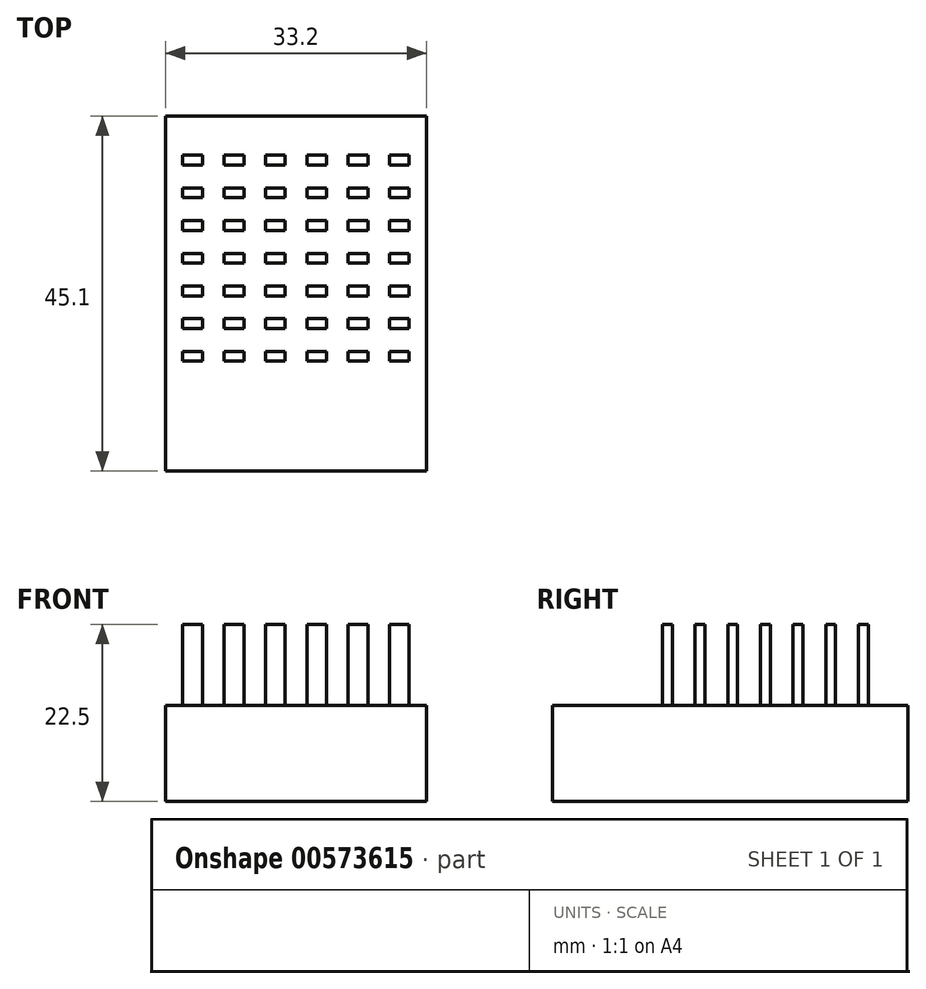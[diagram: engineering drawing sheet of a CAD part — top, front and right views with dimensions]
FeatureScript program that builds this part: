
annotation { "Feature Type Name" : "Feature", "Feature Type Description" : "" }
export const myFeature = defineFeature(function(context is Context, id is Id, definition is map)
    precondition{}
    {
        {
            var Q0;
            Q0=qCreatedBy(makeId("Top.planeOp"),FACE);
            var sketch = newSketch(context, id + "F0", { "sketchPlane" : qUnion([Q0])});
            skLineSegment(sketch, "E0.bottom", {"start": v(16.6, -22.55) * mm, "end": v(-16.6, -22.55) * mm});
            skLineSegment(sketch, "E0.top", {"start": v(16.6, 22.55) * mm, "end": v(-16.6, 22.55) * mm});
            skLineSegment(sketch, "E0.left", {"start": v(16.6, -22.55) * mm, "end": v(16.6, 22.55) * mm});
            skLineSegment(sketch, "E0.right", {"start": v(-16.6, -22.55) * mm, "end": v(-16.6, 22.55) * mm});
            skPoint(sketch, "E0.middle", {"position": v(0, 0) * mm});
            skSolve(sketch);
        }
        {
            var Q0;
            Q0 = qSketchRegion(id + "F0", true);
            extrude(context, id + "F1", {"entities" : qUnion([Q0]), "depth" : 12.2 * mm, "offsetDistance" : 25 * mm});
        }
        {
            var Q0;
            Q0=makeQuery(id+"F1.opExtrude","CAP_FACE",FACE,{"disambiguationData":[OSD([sQuery(id+"F0.wireOp",EDGE,"E0.bottom"),sQuery(id+"F0.wireOp",EDGE,"E0.top"),sQuery(id+"F0.wireOp",EDGE,"E0.left"),sQuery(id+"F0.wireOp",EDGE,"E0.right")])],"isStart":false});
            var sketch = newSketch(context, id + "F2", { "sketchPlane" : qUnion([Q0])});
            skLineSegment(sketch, "E1.bottom", {"start": v(-11.88, 16.3) * mm, "end": v(-14.38, 16.3) * mm});
            skLineSegment(sketch, "E1.top", {"start": v(-11.88, 17.55) * mm, "end": v(-14.38, 17.55) * mm});
            skLineSegment(sketch, "E1.left", {"start": v(-11.88, 16.3) * mm, "end": v(-11.88, 17.55) * mm});
            skLineSegment(sketch, "E1.right", {"start": v(-14.38, 16.3) * mm, "end": v(-14.38, 17.55) * mm});
            skPoint(sketch, "E1.middle", {"position": v(-13.13, 16.93) * mm});
            skPoint(sketch, "E2.0.1.0", {"position": v(-13.13, 12.78) * mm});
            skLineSegment(sketch, "E2.0.1.1", {"start": v(-11.88, 13.4) * mm, "end": v(-14.38, 13.4) * mm});
            skLineSegment(sketch, "E2.0.1.2", {"start": v(-11.88, 12.15) * mm, "end": v(-14.38, 12.15) * mm});
            skLineSegment(sketch, "E2.0.1.3", {"start": v(-14.38, 12.15) * mm, "end": v(-14.38, 13.4) * mm});
            skLineSegment(sketch, "E2.0.1.4", {"start": v(-11.88, 12.15) * mm, "end": v(-11.88, 13.4) * mm});
            skPoint(sketch, "E2.0.2.0", {"position": v(-13.13, 8.62) * mm});
            skLineSegment(sketch, "E2.0.2.1", {"start": v(-11.88, 9.25) * mm, "end": v(-14.38, 9.25) * mm});
            skLineSegment(sketch, "E2.0.2.2", {"start": v(-11.88, 8) * mm, "end": v(-14.38, 8) * mm});
            skLineSegment(sketch, "E2.0.2.3", {"start": v(-14.38, 8) * mm, "end": v(-14.38, 9.25) * mm});
            skLineSegment(sketch, "E2.0.2.4", {"start": v(-11.88, 8) * mm, "end": v(-11.88, 9.25) * mm});
            skPoint(sketch, "E2.0.3.0", {"position": v(-13.13, 4.47) * mm});
            skLineSegment(sketch, "E2.0.3.1", {"start": v(-11.88, 5.1) * mm, "end": v(-14.38, 5.1) * mm});
            skLineSegment(sketch, "E2.0.3.2", {"start": v(-11.88, 3.85) * mm, "end": v(-14.38, 3.85) * mm});
            skLineSegment(sketch, "E2.0.3.3", {"start": v(-14.38, 3.85) * mm, "end": v(-14.38, 5.1) * mm});
            skLineSegment(sketch, "E2.0.3.4", {"start": v(-11.88, 3.85) * mm, "end": v(-11.88, 5.1) * mm});
            skPoint(sketch, "E2.0.4.0", {"position": v(-13.13, 0.32) * mm});
            skLineSegment(sketch, "E2.0.4.1", {"start": v(-11.88, 0.95) * mm, "end": v(-14.38, 0.95) * mm});
            skLineSegment(sketch, "E2.0.4.2", {"start": v(-11.88, -0.3) * mm, "end": v(-14.38, -0.3) * mm});
            skLineSegment(sketch, "E2.0.4.3", {"start": v(-14.38, -0.3) * mm, "end": v(-14.38, 0.95) * mm});
            skLineSegment(sketch, "E2.0.4.4", {"start": v(-11.88, -0.3) * mm, "end": v(-11.88, 0.95) * mm});
            skPoint(sketch, "E2.0.5.0", {"position": v(-13.13, -3.83) * mm});
            skLineSegment(sketch, "E2.0.5.1", {"start": v(-11.88, -3.2) * mm, "end": v(-14.38, -3.2) * mm});
            skLineSegment(sketch, "E2.0.5.2", {"start": v(-11.88, -4.45) * mm, "end": v(-14.38, -4.45) * mm});
            skLineSegment(sketch, "E2.0.5.3", {"start": v(-14.38, -4.45) * mm, "end": v(-14.38, -3.2) * mm});
            skLineSegment(sketch, "E2.0.5.4", {"start": v(-11.88, -4.45) * mm, "end": v(-11.88, -3.2) * mm});
            skPoint(sketch, "E2.0.6.0", {"position": v(-13.13, -7.98) * mm});
            skLineSegment(sketch, "E2.0.6.1", {"start": v(-11.88, -7.35) * mm, "end": v(-14.38, -7.35) * mm});
            skLineSegment(sketch, "E2.0.6.2", {"start": v(-11.88, -8.6) * mm, "end": v(-14.38, -8.6) * mm});
            skLineSegment(sketch, "E2.0.6.3", {"start": v(-14.38, -8.6) * mm, "end": v(-14.38, -7.35) * mm});
            skLineSegment(sketch, "E2.0.6.4", {"start": v(-11.88, -8.6) * mm, "end": v(-11.88, -7.35) * mm});
            skPoint(sketch, "E2.1.0.0", {"position": v(-7.88, 16.93) * mm});
            skLineSegment(sketch, "E2.1.0.1", {"start": v(-6.63, 17.55) * mm, "end": v(-9.13, 17.55) * mm});
            skLineSegment(sketch, "E2.1.0.2", {"start": v(-6.63, 16.3) * mm, "end": v(-9.13, 16.3) * mm});
            skLineSegment(sketch, "E2.1.0.3", {"start": v(-9.13, 16.3) * mm, "end": v(-9.13, 17.55) * mm});
            skLineSegment(sketch, "E2.1.0.4", {"start": v(-6.63, 16.3) * mm, "end": v(-6.63, 17.55) * mm});
            skPoint(sketch, "E2.1.1.0", {"position": v(-7.88, 12.78) * mm});
            skLineSegment(sketch, "E2.1.1.1", {"start": v(-6.63, 13.4) * mm, "end": v(-9.13, 13.4) * mm});
            skLineSegment(sketch, "E2.1.1.2", {"start": v(-6.63, 12.15) * mm, "end": v(-9.13, 12.15) * mm});
            skLineSegment(sketch, "E2.1.1.3", {"start": v(-9.13, 12.15) * mm, "end": v(-9.13, 13.4) * mm});
            skLineSegment(sketch, "E2.1.1.4", {"start": v(-6.63, 12.15) * mm, "end": v(-6.63, 13.4) * mm});
            skPoint(sketch, "E2.1.2.0", {"position": v(-7.88, 8.62) * mm});
            skLineSegment(sketch, "E2.1.2.1", {"start": v(-6.63, 9.25) * mm, "end": v(-9.13, 9.25) * mm});
            skLineSegment(sketch, "E2.1.2.2", {"start": v(-6.63, 8) * mm, "end": v(-9.13, 8) * mm});
            skLineSegment(sketch, "E2.1.2.3", {"start": v(-9.13, 8) * mm, "end": v(-9.13, 9.25) * mm});
            skLineSegment(sketch, "E2.1.2.4", {"start": v(-6.63, 8) * mm, "end": v(-6.63, 9.25) * mm});
            skPoint(sketch, "E2.1.3.0", {"position": v(-7.88, 4.47) * mm});
            skLineSegment(sketch, "E2.1.3.1", {"start": v(-6.63, 5.1) * mm, "end": v(-9.13, 5.1) * mm});
            skLineSegment(sketch, "E2.1.3.2", {"start": v(-6.63, 3.85) * mm, "end": v(-9.13, 3.85) * mm});
            skLineSegment(sketch, "E2.1.3.3", {"start": v(-9.13, 3.85) * mm, "end": v(-9.13, 5.1) * mm});
            skLineSegment(sketch, "E2.1.3.4", {"start": v(-6.63, 3.85) * mm, "end": v(-6.63, 5.1) * mm});
            skPoint(sketch, "E2.1.4.0", {"position": v(-7.88, 0.32) * mm});
            skLineSegment(sketch, "E2.1.4.1", {"start": v(-6.63, 0.95) * mm, "end": v(-9.13, 0.95) * mm});
            skLineSegment(sketch, "E2.1.4.2", {"start": v(-6.63, -0.3) * mm, "end": v(-9.13, -0.3) * mm});
            skLineSegment(sketch, "E2.1.4.3", {"start": v(-9.13, -0.3) * mm, "end": v(-9.13, 0.95) * mm});
            skLineSegment(sketch, "E2.1.4.4", {"start": v(-6.63, -0.3) * mm, "end": v(-6.63, 0.95) * mm});
            skPoint(sketch, "E2.1.5.0", {"position": v(-7.88, -3.83) * mm});
            skLineSegment(sketch, "E2.1.5.1", {"start": v(-6.63, -3.2) * mm, "end": v(-9.13, -3.2) * mm});
            skLineSegment(sketch, "E2.1.5.2", {"start": v(-6.63, -4.45) * mm, "end": v(-9.13, -4.45) * mm});
            skLineSegment(sketch, "E2.1.5.3", {"start": v(-9.13, -4.45) * mm, "end": v(-9.13, -3.2) * mm});
            skLineSegment(sketch, "E2.1.5.4", {"start": v(-6.63, -4.45) * mm, "end": v(-6.63, -3.2) * mm});
            skPoint(sketch, "E2.1.6.0", {"position": v(-7.88, -7.98) * mm});
            skLineSegment(sketch, "E2.1.6.1", {"start": v(-6.63, -7.35) * mm, "end": v(-9.13, -7.35) * mm});
            skLineSegment(sketch, "E2.1.6.2", {"start": v(-6.63, -8.6) * mm, "end": v(-9.13, -8.6) * mm});
            skLineSegment(sketch, "E2.1.6.3", {"start": v(-9.13, -8.6) * mm, "end": v(-9.13, -7.35) * mm});
            skLineSegment(sketch, "E2.1.6.4", {"start": v(-6.63, -8.6) * mm, "end": v(-6.63, -7.35) * mm});
            skPoint(sketch, "E2.2.0.0", {"position": v(-2.62, 16.93) * mm});
            skLineSegment(sketch, "E2.2.0.1", {"start": v(-1.37, 17.55) * mm, "end": v(-3.88, 17.55) * mm});
            skLineSegment(sketch, "E2.2.0.2", {"start": v(-1.37, 16.3) * mm, "end": v(-3.88, 16.3) * mm});
            skLineSegment(sketch, "E2.2.0.3", {"start": v(-3.88, 16.3) * mm, "end": v(-3.88, 17.55) * mm});
            skLineSegment(sketch, "E2.2.0.4", {"start": v(-1.38, 16.3) * mm, "end": v(-1.38, 17.55) * mm});
            skPoint(sketch, "E2.2.1.0", {"position": v(-2.62, 12.78) * mm});
            skLineSegment(sketch, "E2.2.1.1", {"start": v(-1.37, 13.4) * mm, "end": v(-3.88, 13.4) * mm});
            skLineSegment(sketch, "E2.2.1.2", {"start": v(-1.37, 12.15) * mm, "end": v(-3.88, 12.15) * mm});
            skLineSegment(sketch, "E2.2.1.3", {"start": v(-3.88, 12.15) * mm, "end": v(-3.88, 13.4) * mm});
            skLineSegment(sketch, "E2.2.1.4", {"start": v(-1.38, 12.15) * mm, "end": v(-1.38, 13.4) * mm});
            skPoint(sketch, "E2.2.2.0", {"position": v(-2.62, 8.62) * mm});
            skLineSegment(sketch, "E2.2.2.1", {"start": v(-1.37, 9.25) * mm, "end": v(-3.88, 9.25) * mm});
            skLineSegment(sketch, "E2.2.2.2", {"start": v(-1.37, 8) * mm, "end": v(-3.88, 8) * mm});
            skLineSegment(sketch, "E2.2.2.3", {"start": v(-3.88, 8) * mm, "end": v(-3.88, 9.25) * mm});
            skLineSegment(sketch, "E2.2.2.4", {"start": v(-1.38, 8) * mm, "end": v(-1.38, 9.25) * mm});
            skPoint(sketch, "E2.2.3.0", {"position": v(-2.62, 4.47) * mm});
            skLineSegment(sketch, "E2.2.3.1", {"start": v(-1.37, 5.1) * mm, "end": v(-3.88, 5.1) * mm});
            skLineSegment(sketch, "E2.2.3.2", {"start": v(-1.37, 3.85) * mm, "end": v(-3.88, 3.85) * mm});
            skLineSegment(sketch, "E2.2.3.3", {"start": v(-3.88, 3.85) * mm, "end": v(-3.88, 5.1) * mm});
            skLineSegment(sketch, "E2.2.3.4", {"start": v(-1.38, 3.85) * mm, "end": v(-1.38, 5.1) * mm});
            skPoint(sketch, "E2.2.4.0", {"position": v(-2.62, 0.32) * mm});
            skLineSegment(sketch, "E2.2.4.1", {"start": v(-1.37, 0.95) * mm, "end": v(-3.88, 0.95) * mm});
            skLineSegment(sketch, "E2.2.4.2", {"start": v(-1.37, -0.3) * mm, "end": v(-3.88, -0.3) * mm});
            skLineSegment(sketch, "E2.2.4.3", {"start": v(-3.88, -0.3) * mm, "end": v(-3.88, 0.95) * mm});
            skLineSegment(sketch, "E2.2.4.4", {"start": v(-1.38, -0.3) * mm, "end": v(-1.38, 0.95) * mm});
            skPoint(sketch, "E2.2.5.0", {"position": v(-2.62, -3.83) * mm});
            skLineSegment(sketch, "E2.2.5.1", {"start": v(-1.37, -3.2) * mm, "end": v(-3.88, -3.2) * mm});
            skLineSegment(sketch, "E2.2.5.2", {"start": v(-1.37, -4.45) * mm, "end": v(-3.88, -4.45) * mm});
            skLineSegment(sketch, "E2.2.5.3", {"start": v(-3.88, -4.45) * mm, "end": v(-3.88, -3.2) * mm});
            skLineSegment(sketch, "E2.2.5.4", {"start": v(-1.38, -4.45) * mm, "end": v(-1.38, -3.2) * mm});
            skPoint(sketch, "E2.2.6.0", {"position": v(-2.62, -7.98) * mm});
            skLineSegment(sketch, "E2.2.6.1", {"start": v(-1.37, -7.35) * mm, "end": v(-3.88, -7.35) * mm});
            skLineSegment(sketch, "E2.2.6.2", {"start": v(-1.37, -8.6) * mm, "end": v(-3.88, -8.6) * mm});
            skLineSegment(sketch, "E2.2.6.3", {"start": v(-3.88, -8.6) * mm, "end": v(-3.88, -7.35) * mm});
            skLineSegment(sketch, "E2.2.6.4", {"start": v(-1.38, -8.6) * mm, "end": v(-1.38, -7.35) * mm});
            skPoint(sketch, "E2.3.0.0", {"position": v(2.63, 16.93) * mm});
            skLineSegment(sketch, "E2.3.0.1", {"start": v(3.88, 17.55) * mm, "end": v(1.38, 17.55) * mm});
            skLineSegment(sketch, "E2.3.0.2", {"start": v(3.88, 16.3) * mm, "end": v(1.38, 16.3) * mm});
            skLineSegment(sketch, "E2.3.0.3", {"start": v(1.37, 16.3) * mm, "end": v(1.37, 17.55) * mm});
            skLineSegment(sketch, "E2.3.0.4", {"start": v(3.87, 16.3) * mm, "end": v(3.87, 17.55) * mm});
            skPoint(sketch, "E2.3.1.0", {"position": v(2.63, 12.78) * mm});
            skLineSegment(sketch, "E2.3.1.1", {"start": v(3.88, 13.4) * mm, "end": v(1.38, 13.4) * mm});
            skLineSegment(sketch, "E2.3.1.2", {"start": v(3.88, 12.15) * mm, "end": v(1.38, 12.15) * mm});
            skLineSegment(sketch, "E2.3.1.3", {"start": v(1.37, 12.15) * mm, "end": v(1.37, 13.4) * mm});
            skLineSegment(sketch, "E2.3.1.4", {"start": v(3.87, 12.15) * mm, "end": v(3.87, 13.4) * mm});
            skPoint(sketch, "E2.3.2.0", {"position": v(2.63, 8.62) * mm});
            skLineSegment(sketch, "E2.3.2.1", {"start": v(3.88, 9.25) * mm, "end": v(1.38, 9.25) * mm});
            skLineSegment(sketch, "E2.3.2.2", {"start": v(3.88, 8) * mm, "end": v(1.38, 8) * mm});
            skLineSegment(sketch, "E2.3.2.3", {"start": v(1.37, 8) * mm, "end": v(1.37, 9.25) * mm});
            skLineSegment(sketch, "E2.3.2.4", {"start": v(3.87, 8) * mm, "end": v(3.87, 9.25) * mm});
            skPoint(sketch, "E2.3.3.0", {"position": v(2.63, 4.47) * mm});
            skLineSegment(sketch, "E2.3.3.1", {"start": v(3.88, 5.1) * mm, "end": v(1.38, 5.1) * mm});
            skLineSegment(sketch, "E2.3.3.2", {"start": v(3.88, 3.85) * mm, "end": v(1.38, 3.85) * mm});
            skLineSegment(sketch, "E2.3.3.3", {"start": v(1.37, 3.85) * mm, "end": v(1.37, 5.1) * mm});
            skLineSegment(sketch, "E2.3.3.4", {"start": v(3.87, 3.85) * mm, "end": v(3.87, 5.1) * mm});
            skPoint(sketch, "E2.3.4.0", {"position": v(2.63, 0.32) * mm});
            skLineSegment(sketch, "E2.3.4.1", {"start": v(3.88, 0.95) * mm, "end": v(1.38, 0.95) * mm});
            skLineSegment(sketch, "E2.3.4.2", {"start": v(3.88, -0.3) * mm, "end": v(1.38, -0.3) * mm});
            skLineSegment(sketch, "E2.3.4.3", {"start": v(1.37, -0.3) * mm, "end": v(1.37, 0.95) * mm});
            skLineSegment(sketch, "E2.3.4.4", {"start": v(3.87, -0.3) * mm, "end": v(3.87, 0.95) * mm});
            skPoint(sketch, "E2.3.5.0", {"position": v(2.63, -3.83) * mm});
            skLineSegment(sketch, "E2.3.5.1", {"start": v(3.88, -3.2) * mm, "end": v(1.38, -3.2) * mm});
            skLineSegment(sketch, "E2.3.5.2", {"start": v(3.88, -4.45) * mm, "end": v(1.38, -4.45) * mm});
            skLineSegment(sketch, "E2.3.5.3", {"start": v(1.37, -4.45) * mm, "end": v(1.37, -3.2) * mm});
            skLineSegment(sketch, "E2.3.5.4", {"start": v(3.87, -4.45) * mm, "end": v(3.87, -3.2) * mm});
            skPoint(sketch, "E2.3.6.0", {"position": v(2.63, -7.98) * mm});
            skLineSegment(sketch, "E2.3.6.1", {"start": v(3.88, -7.35) * mm, "end": v(1.38, -7.35) * mm});
            skLineSegment(sketch, "E2.3.6.2", {"start": v(3.88, -8.6) * mm, "end": v(1.38, -8.6) * mm});
            skLineSegment(sketch, "E2.3.6.3", {"start": v(1.37, -8.6) * mm, "end": v(1.37, -7.35) * mm});
            skLineSegment(sketch, "E2.3.6.4", {"start": v(3.87, -8.6) * mm, "end": v(3.87, -7.35) * mm});
            skPoint(sketch, "E2.4.0.0", {"position": v(7.88, 16.93) * mm});
            skLineSegment(sketch, "E2.4.0.1", {"start": v(9.13, 17.55) * mm, "end": v(6.63, 17.55) * mm});
            skLineSegment(sketch, "E2.4.0.2", {"start": v(9.13, 16.3) * mm, "end": v(6.63, 16.3) * mm});
            skLineSegment(sketch, "E2.4.0.3", {"start": v(6.62, 16.3) * mm, "end": v(6.62, 17.55) * mm});
            skLineSegment(sketch, "E2.4.0.4", {"start": v(9.12, 16.3) * mm, "end": v(9.12, 17.55) * mm});
            skPoint(sketch, "E2.4.1.0", {"position": v(7.88, 12.78) * mm});
            skLineSegment(sketch, "E2.4.1.1", {"start": v(9.13, 13.4) * mm, "end": v(6.63, 13.4) * mm});
            skLineSegment(sketch, "E2.4.1.2", {"start": v(9.13, 12.15) * mm, "end": v(6.63, 12.15) * mm});
            skLineSegment(sketch, "E2.4.1.3", {"start": v(6.62, 12.15) * mm, "end": v(6.62, 13.4) * mm});
            skLineSegment(sketch, "E2.4.1.4", {"start": v(9.12, 12.15) * mm, "end": v(9.12, 13.4) * mm});
            skPoint(sketch, "E2.4.2.0", {"position": v(7.88, 8.62) * mm});
            skLineSegment(sketch, "E2.4.2.1", {"start": v(9.13, 9.25) * mm, "end": v(6.63, 9.25) * mm});
            skLineSegment(sketch, "E2.4.2.2", {"start": v(9.13, 8) * mm, "end": v(6.63, 8) * mm});
            skLineSegment(sketch, "E2.4.2.3", {"start": v(6.62, 8) * mm, "end": v(6.62, 9.25) * mm});
            skLineSegment(sketch, "E2.4.2.4", {"start": v(9.12, 8) * mm, "end": v(9.12, 9.25) * mm});
            skPoint(sketch, "E2.4.3.0", {"position": v(7.88, 4.47) * mm});
            skLineSegment(sketch, "E2.4.3.1", {"start": v(9.13, 5.1) * mm, "end": v(6.63, 5.1) * mm});
            skLineSegment(sketch, "E2.4.3.2", {"start": v(9.13, 3.85) * mm, "end": v(6.63, 3.85) * mm});
            skLineSegment(sketch, "E2.4.3.3", {"start": v(6.62, 3.85) * mm, "end": v(6.62, 5.1) * mm});
            skLineSegment(sketch, "E2.4.3.4", {"start": v(9.12, 3.85) * mm, "end": v(9.12, 5.1) * mm});
            skPoint(sketch, "E2.4.4.0", {"position": v(7.88, 0.32) * mm});
            skLineSegment(sketch, "E2.4.4.1", {"start": v(9.13, 0.95) * mm, "end": v(6.63, 0.95) * mm});
            skLineSegment(sketch, "E2.4.4.2", {"start": v(9.13, -0.3) * mm, "end": v(6.63, -0.3) * mm});
            skLineSegment(sketch, "E2.4.4.3", {"start": v(6.62, -0.3) * mm, "end": v(6.62, 0.95) * mm});
            skLineSegment(sketch, "E2.4.4.4", {"start": v(9.12, -0.3) * mm, "end": v(9.12, 0.95) * mm});
            skPoint(sketch, "E2.4.5.0", {"position": v(7.88, -3.83) * mm});
            skLineSegment(sketch, "E2.4.5.1", {"start": v(9.13, -3.2) * mm, "end": v(6.63, -3.2) * mm});
            skLineSegment(sketch, "E2.4.5.2", {"start": v(9.13, -4.45) * mm, "end": v(6.63, -4.45) * mm});
            skLineSegment(sketch, "E2.4.5.3", {"start": v(6.62, -4.45) * mm, "end": v(6.62, -3.2) * mm});
            skLineSegment(sketch, "E2.4.5.4", {"start": v(9.12, -4.45) * mm, "end": v(9.12, -3.2) * mm});
            skPoint(sketch, "E2.4.6.0", {"position": v(7.88, -7.98) * mm});
            skLineSegment(sketch, "E2.4.6.1", {"start": v(9.13, -7.35) * mm, "end": v(6.63, -7.35) * mm});
            skLineSegment(sketch, "E2.4.6.2", {"start": v(9.13, -8.6) * mm, "end": v(6.63, -8.6) * mm});
            skLineSegment(sketch, "E2.4.6.3", {"start": v(6.62, -8.6) * mm, "end": v(6.62, -7.35) * mm});
            skLineSegment(sketch, "E2.4.6.4", {"start": v(9.12, -8.6) * mm, "end": v(9.12, -7.35) * mm});
            skPoint(sketch, "E2.5.0.0", {"position": v(13.13, 16.93) * mm});
            skLineSegment(sketch, "E2.5.0.1", {"start": v(14.38, 17.55) * mm, "end": v(11.88, 17.55) * mm});
            skLineSegment(sketch, "E2.5.0.2", {"start": v(14.38, 16.3) * mm, "end": v(11.88, 16.3) * mm});
            skLineSegment(sketch, "E2.5.0.3", {"start": v(11.87, 16.3) * mm, "end": v(11.87, 17.55) * mm});
            skLineSegment(sketch, "E2.5.0.4", {"start": v(14.37, 16.3) * mm, "end": v(14.37, 17.55) * mm});
            skPoint(sketch, "E2.5.1.0", {"position": v(13.13, 12.78) * mm});
            skLineSegment(sketch, "E2.5.1.1", {"start": v(14.38, 13.4) * mm, "end": v(11.88, 13.4) * mm});
            skLineSegment(sketch, "E2.5.1.2", {"start": v(14.38, 12.15) * mm, "end": v(11.88, 12.15) * mm});
            skLineSegment(sketch, "E2.5.1.3", {"start": v(11.87, 12.15) * mm, "end": v(11.87, 13.4) * mm});
            skLineSegment(sketch, "E2.5.1.4", {"start": v(14.37, 12.15) * mm, "end": v(14.37, 13.4) * mm});
            skPoint(sketch, "E2.5.2.0", {"position": v(13.13, 8.62) * mm});
            skLineSegment(sketch, "E2.5.2.1", {"start": v(14.38, 9.25) * mm, "end": v(11.88, 9.25) * mm});
            skLineSegment(sketch, "E2.5.2.2", {"start": v(14.38, 8) * mm, "end": v(11.88, 8) * mm});
            skLineSegment(sketch, "E2.5.2.3", {"start": v(11.87, 8) * mm, "end": v(11.87, 9.25) * mm});
            skLineSegment(sketch, "E2.5.2.4", {"start": v(14.37, 8) * mm, "end": v(14.37, 9.25) * mm});
            skPoint(sketch, "E2.5.3.0", {"position": v(13.13, 4.47) * mm});
            skLineSegment(sketch, "E2.5.3.1", {"start": v(14.38, 5.1) * mm, "end": v(11.88, 5.1) * mm});
            skLineSegment(sketch, "E2.5.3.2", {"start": v(14.38, 3.85) * mm, "end": v(11.88, 3.85) * mm});
            skLineSegment(sketch, "E2.5.3.3", {"start": v(11.87, 3.85) * mm, "end": v(11.87, 5.1) * mm});
            skLineSegment(sketch, "E2.5.3.4", {"start": v(14.37, 3.85) * mm, "end": v(14.37, 5.1) * mm});
            skPoint(sketch, "E2.5.4.0", {"position": v(13.13, 0.32) * mm});
            skLineSegment(sketch, "E2.5.4.1", {"start": v(14.38, 0.95) * mm, "end": v(11.88, 0.95) * mm});
            skLineSegment(sketch, "E2.5.4.2", {"start": v(14.38, -0.3) * mm, "end": v(11.88, -0.3) * mm});
            skLineSegment(sketch, "E2.5.4.3", {"start": v(11.87, -0.3) * mm, "end": v(11.87, 0.95) * mm});
            skLineSegment(sketch, "E2.5.4.4", {"start": v(14.37, -0.3) * mm, "end": v(14.37, 0.95) * mm});
            skPoint(sketch, "E2.5.5.0", {"position": v(13.13, -3.83) * mm});
            skLineSegment(sketch, "E2.5.5.1", {"start": v(14.38, -3.2) * mm, "end": v(11.88, -3.2) * mm});
            skLineSegment(sketch, "E2.5.5.2", {"start": v(14.38, -4.45) * mm, "end": v(11.88, -4.45) * mm});
            skLineSegment(sketch, "E2.5.5.3", {"start": v(11.87, -4.45) * mm, "end": v(11.87, -3.2) * mm});
            skLineSegment(sketch, "E2.5.5.4", {"start": v(14.37, -4.45) * mm, "end": v(14.37, -3.2) * mm});
            skPoint(sketch, "E2.5.6.0", {"position": v(13.13, -7.98) * mm});
            skLineSegment(sketch, "E2.5.6.1", {"start": v(14.38, -7.35) * mm, "end": v(11.88, -7.35) * mm});
            skLineSegment(sketch, "E2.5.6.2", {"start": v(14.38, -8.6) * mm, "end": v(11.88, -8.6) * mm});
            skLineSegment(sketch, "E2.5.6.3", {"start": v(11.87, -8.6) * mm, "end": v(11.87, -7.35) * mm});
            skLineSegment(sketch, "E2.5.6.4", {"start": v(14.37, -8.6) * mm, "end": v(14.37, -7.35) * mm});
            skLineSegment(sketch, "E2.direction1", {"start": v(-14.38, 16.3) * mm, "end": v(-9.13, 16.3) * mm, "construction": true});
            skLineSegment(sketch, "E2.direction2", {"start": v(-14.38, 16.3) * mm, "end": v(-14.38, 12.15) * mm, "construction": true});
            skLineSegment(sketch, "E3.bottom", {"start": v(-14.38, 17.55) * mm, "end": v(14.38, 17.55) * mm, "construction": true});
            skLineSegment(sketch, "E3.top", {"start": v(-14.38, -8.6) * mm, "end": v(14.38, -8.6) * mm, "construction": true});
            skLineSegment(sketch, "E3.left", {"start": v(-14.38, 17.55) * mm, "end": v(-14.38, -8.6) * mm, "construction": true});
            skLineSegment(sketch, "E3.right", {"start": v(14.38, 17.55) * mm, "end": v(14.38, -8.6) * mm, "construction": true});
            skLineSegment(sketch, "E4", {"start": v(0, 17.55) * mm, "end": v(0, -8.6) * mm, "construction": true});
            skLineSegment(sketch, "E5", {"start": v(-14.38, 4.47) * mm, "end": v(14.38, 4.47) * mm, "construction": true});
            skPoint(sketch, "E6", {"position": v(0, 4.47) * mm});
            skSolve(sketch);
        }
        {
            var Q0;
            Q0 = qSketchRegion(id + "F2", true);
            extrude(context, id + "F3", {"entities" : qUnion([Q0]), "operationType" : NewBodyOperationType.ADD, "depth" : 10.3 * mm, "offsetDistance" : 25 * mm});
        }
    });
